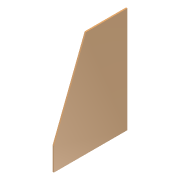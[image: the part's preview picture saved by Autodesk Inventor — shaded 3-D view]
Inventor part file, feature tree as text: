
AUTODESK INVENTOR PART (.ipt)
format: ipt  version: 2014 (Build 180170000, 170)  size: 76,288 bytes
history: native  units: mm
features: extrude x1, sketch x1
ambient origin geometry x8: Origin, YZ Plane, XZ Plane, XY Plane, X Axis, Y Axis, Z Axis, Center Point
bodies: Solid1 (feature_tree)
feature tree (2):
  extrude  "Extrusion1"  Depth=230.0mm
  sketch  "Sketch1"  dims[d0=160.0mm d1=230.0mm d2=90.0mm d3=50.0mm d4=3.0mm d5=0.0mm]
